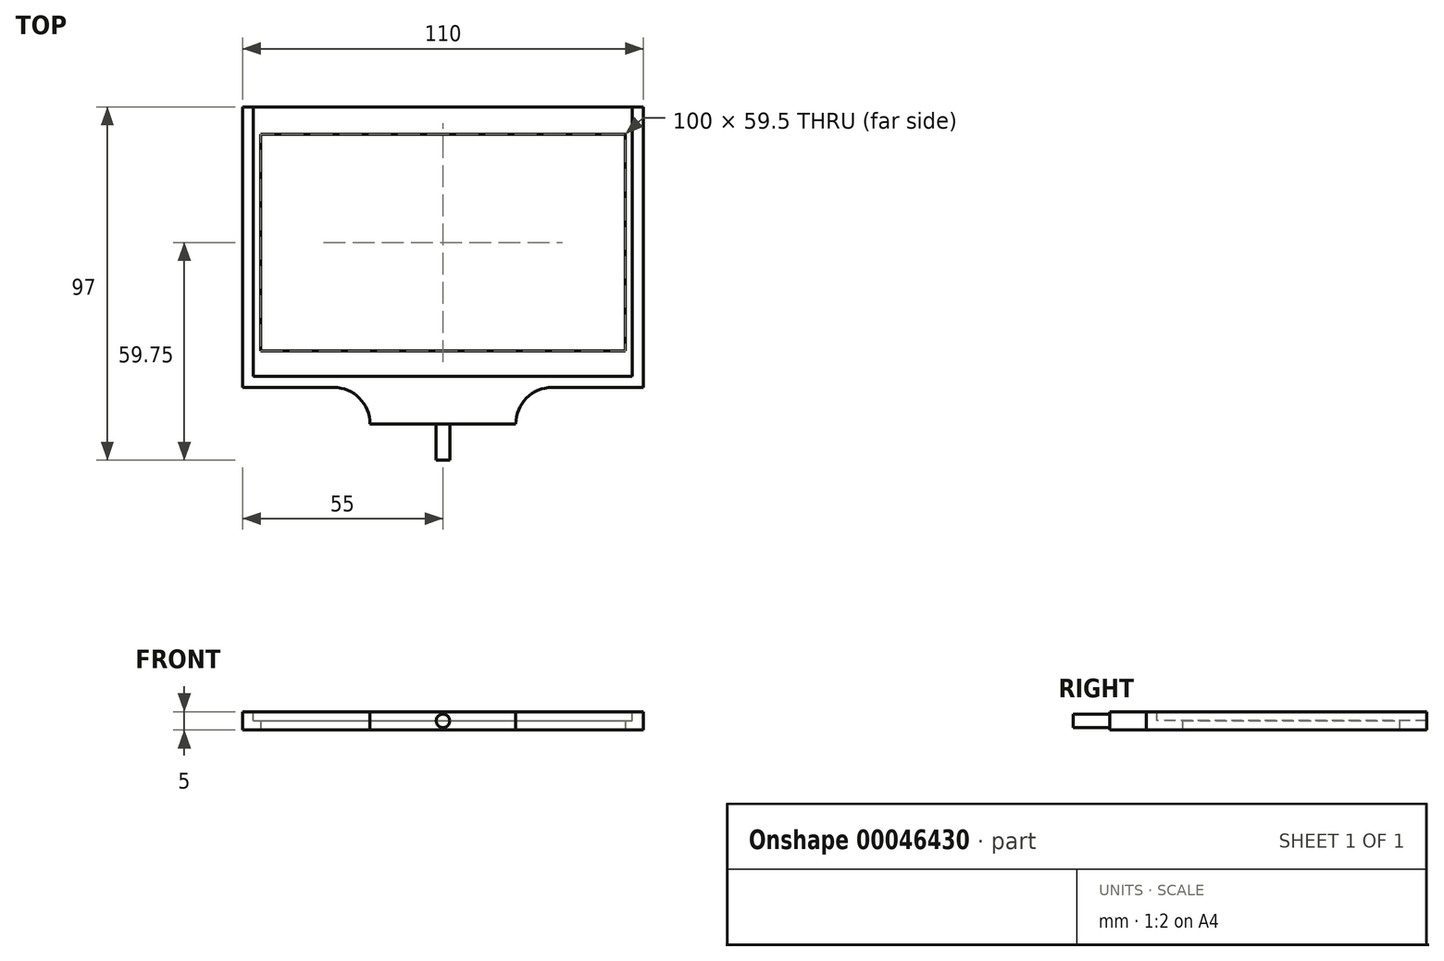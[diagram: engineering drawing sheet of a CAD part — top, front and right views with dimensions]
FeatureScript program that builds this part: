
annotation { "Feature Type Name" : "Feature", "Feature Type Description" : "" }
export const myFeature = defineFeature(function(context is Context, id is Id, definition is map)
    precondition{}
    {
        {
            var Q0;
            Q0=qCreatedBy(makeId("Top.planeOp"),FACE);
            var sketch = newSketch(context, id + "F0", { "sketchPlane" : qUnion([Q0])});
            skLineSegment(sketch, "E0.bottom", {"start": v(-55, 0) * mm, "end": v(55, 0) * mm});
            skLineSegment(sketch, "E0.top", {"start": v(-55, 77) * mm, "end": v(55, 77) * mm});
            skLineSegment(sketch, "E0.left", {"start": v(-55, 0) * mm, "end": v(-55, 77) * mm});
            skLineSegment(sketch, "E0.right", {"start": v(55, 0) * mm, "end": v(55, 77) * mm});
            skLineSegment(sketch, "E1.0", {"start": v(-50, 10) * mm, "end": v(50, 10) * mm});
            skLineSegment(sketch, "E1.1", {"start": v(-50, 10) * mm, "end": v(-50, 69.5) * mm});
            skLineSegment(sketch, "E1.2", {"start": v(-50, 69.5) * mm, "end": v(50, 69.5) * mm});
            skLineSegment(sketch, "E1.3", {"start": v(50, 10) * mm, "end": v(50, 69.5) * mm});
            skLineSegment(sketch, "E2.bottom", {"start": v(-20, 0) * mm, "end": v(20, 0) * mm});
            skLineSegment(sketch, "E2.top", {"start": v(-20, -10) * mm, "end": v(20, -10) * mm});
            skLineSegment(sketch, "E2.left", {"start": v(-20, 0) * mm, "end": v(-20, -10) * mm});
            skLineSegment(sketch, "E2.right", {"start": v(20, 0) * mm, "end": v(20, -10) * mm});
            skSolve(sketch);
        }
        {
            var Q0;
            Q0=makeQuery(id+"F0.imprint","IMPRINT",FACE,{"disambiguationData":[TD([[makeQuery(id+"F0.imprint","IMPRINT",EDGE,{"derivedFrom":sQuery(id+"F0.wireOp",EDGE,"E0.bottom")}),1.0]])]});
            var Q1;
            Q1=makeQuery(id+"F0.imprint","IMPRINT",FACE,{"disambiguationData":[TD([[makeQuery(id+"F0.imprint","IMPRINT",EDGE,{"derivedFrom":sQuery(id+"F0.wireOp",EDGE,"E2.top")}),1.0]])]});
            extrude(context, id + "F1", {"entities" : qUnion([Q0, Q1]), "depth" : 5 * mm, "offsetDistance" : 25 * mm});
        }
        {
            var Q0;
            Q0=makeQuery(id+"F1.opExtrude","CAP_FACE",FACE,{"disambiguationData":[OSD([sQuery(id+"F0.wireOp",EDGE,"E0.bottom"),sQuery(id+"F0.wireOp",EDGE,"E0.top"),sQuery(id+"F0.wireOp",EDGE,"E0.left"),sQuery(id+"F0.wireOp",EDGE,"E0.right"),sQuery(id+"F0.wireOp",EDGE,"E1.0"),sQuery(id+"F0.wireOp",EDGE,"E1.1"),sQuery(id+"F0.wireOp",EDGE,"E1.2"),sQuery(id+"F0.wireOp",EDGE,"E1.3"),sQuery(id+"F0.wireOp",EDGE,"E2.top"),sQuery(id+"F0.wireOp",EDGE,"E2.left"),sQuery(id+"F0.wireOp",EDGE,"E2.right")])],"isStart":false});
            var sketch = newSketch(context, id + "F2", { "sketchPlane" : qUnion([Q0])});
            skLineSegment(sketch, "E3", {"start": v(-52, 77) * mm, "end": v(-52, 3) * mm});
            skLineSegment(sketch, "E4", {"start": v(-52, 3) * mm, "end": v(52, 3) * mm});
            skLineSegment(sketch, "E5", {"start": v(52, 3) * mm, "end": v(52, 77) * mm});
            skLineSegment(sketch, "E6", {"start": v(52, 77) * mm, "end": v(-52, 77) * mm});
            skSolve(sketch);
        }
        {
            var Q0;
            Q0=makeQuery(id+"F2.imprint","IMPRINT",FACE,{"disambiguationData":[TD([[makeQuery(id+"F2.imprint","IMPRINT",EDGE,{"derivedFrom":sQuery(id+"F2.wireOp",EDGE,"E3")}),1.0]])]});
            extrude(context, id + "F3", {"entities" : qUnion([Q0]), "operationType" : NewBodyOperationType.REMOVE, "oppositeDirection" : true, "depth" : 2.5 * mm, "offsetDistance" : 25 * mm});
        }
        {
            var Q0;
            Q0=makeQuery(id+"F1.opExtrude","SWEPT_FACE",FACE,{"disambiguationData":[OSD([sQuery(id+"F0.wireOp",EDGE,"E2.top")])]});
            var sketch = newSketch(context, id + "F4", { "sketchPlane" : qUnion([Q0])});
            skCircle(sketch, "E7", {"center": v(0, 2.5) * mm, "radius": 1.85 * mm});
            skSolve(sketch);
        }
        {
            var Q0;
            Q0=makeQuery(id+"F4.imprint","IMPRINT",FACE,{"disambiguationData":[TD([[makeQuery(id+"F4.imprint","IMPRINT",EDGE,{"derivedFrom":sQuery(id+"F4.wireOp",EDGE,"E7")}),1.0]])]});
            extrude(context, id + "F5", {"entities" : qUnion([Q0]), "operationType" : NewBodyOperationType.ADD, "depth" : 10 * mm, "offsetDistance" : 25 * mm});
        }
        {
            var Q0;
            Q0=makeQuery(id+"F1.opExtrude","SWEPT_EDGE",EDGE,{"disambiguationData":[OSD([sQuery(id+"F0.wireOp",EDGE,"E0.bottom"),sQuery(id+"F0.wireOp",EDGE,"E2.right")])]});
            var Q1;
            Q1=makeQuery(id+"F1.opExtrude","SWEPT_EDGE",EDGE,{"disambiguationData":[OSD([sQuery(id+"F0.wireOp",EDGE,"E0.bottom"),sQuery(id+"F0.wireOp",EDGE,"E2.left")])]});
            fillet(context, id + "F6", {"entities" : qUnion([Q0, Q1]), "tangentPropagation" : true, "radius" : 10 * mm, "defaultsChanged" : false, "vertexSettings" : [], "allowEdgeOverflow" : false});
        }
    });
